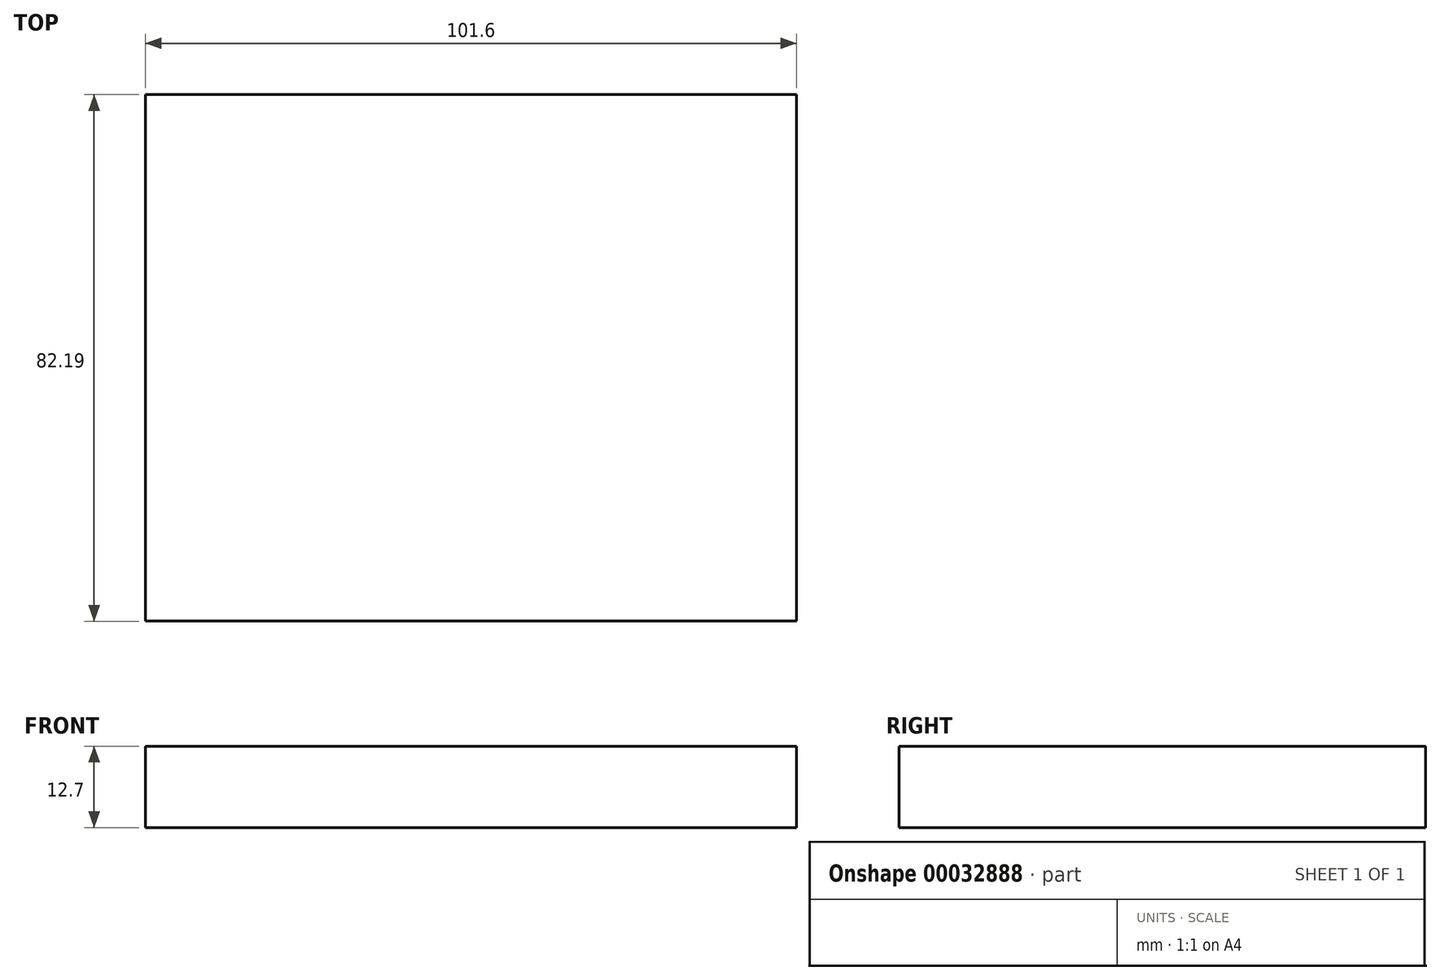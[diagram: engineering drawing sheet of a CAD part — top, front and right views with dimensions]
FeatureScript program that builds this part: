
annotation { "Feature Type Name" : "Feature", "Feature Type Description" : "" }
export const myFeature = defineFeature(function(context is Context, id is Id, definition is map)
    precondition{}
    {
        {
            var Q0;
            Q0=qCreatedBy(makeId("Top.planeOp"),FACE);
            var sketch = newSketch(context, id + "F0", { "sketchPlane" : qUnion([Q0])});
            skLineSegment(sketch, "E0.bottom", {"start": v(-44.28, 36.24) * mm, "end": v(57.32, 36.24) * mm});
            skLineSegment(sketch, "E0.top", {"start": v(-44.28, -45.95) * mm, "end": v(57.32, -45.95) * mm});
            skLineSegment(sketch, "E0.left", {"start": v(-44.28, 36.24) * mm, "end": v(-44.28, -45.95) * mm});
            skLineSegment(sketch, "E0.right", {"start": v(57.32, 36.24) * mm, "end": v(57.32, -45.95) * mm});
            skSolve(sketch);
        }
        {
            var Q0;
            Q0 = qSketchRegion(id + "F0", true);
            extrude(context, id + "F1", {"entities" : qUnion([Q0]), "depth" : 12.7 * mm});
        }
    });
